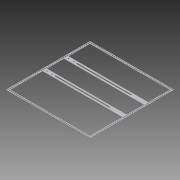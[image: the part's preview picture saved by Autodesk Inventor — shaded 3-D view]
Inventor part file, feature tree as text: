
AUTODESK INVENTOR PART (.ipt)
format: ipt  version: 2013 (Build 170138000, 138)  size: 9,560,576 bytes
history: native  units: in
note: dims shown in document units (in); Inventor stores cm internally (conversion verified against a paired STEP export)
features: reference x4, sketch x3, other x3, sheet_metal_op x2, extrude x1
ambient origin geometry x8: Origin, YZ Plane, XZ Plane, XY Plane, X Axis, Y Axis, Z Axis, Center Point
feature tree (13):
  extrude  "Extrusion2"  Depth=0.5in
  sheet_metal_op  "Face1"
  sketch  "Sketch2"  dims[d0=0.5in d3=0.5in]
  other  "Plate1"
  sheet_metal_op  "Bend1"
  sketch  "Sketch8"  dims[d4=0.5in]
  sketch  "Sketch9"  dims[d6=15.5in d7=14.1732in d9=0.4357in d10=0.3937in d12=1.0in d14=13.7795in d16=0.4357in d17=0.3937in d19=1.0in d21=19.25in d22=19.685in d24=0.3878in d25=0.3937in d27=1.0in d36=15.5in d42=0.4357in d43=0.25in d44=14.1732in d46=0.4357in d47=0.3937in d49=1.0in d51=18.5in d52=9.25in d53=0.125in d54=0.0in d55=1.0in d58=1.0in d59=5.0in d60=4.0in d61=0.125in d62=0.125in d63=0.0625in d64=0.25in d65=0.125in d96=0.266in d97=0.5in d98=3.5in d99=0.266in d100=0.5in d101=3.0in d102=0.266in d103=3.5in d104=0.5in d105=0.266in d106=0.5in d107=3.0in d108=0.125in d109=0.0in d110=0.125in d111=0.0in]
  reference  "Reference4"
  reference  "Reference5"
  reference  "Reference6"
  reference  "Reference7"
  other  "Cut6"
  other  "Cut7"
